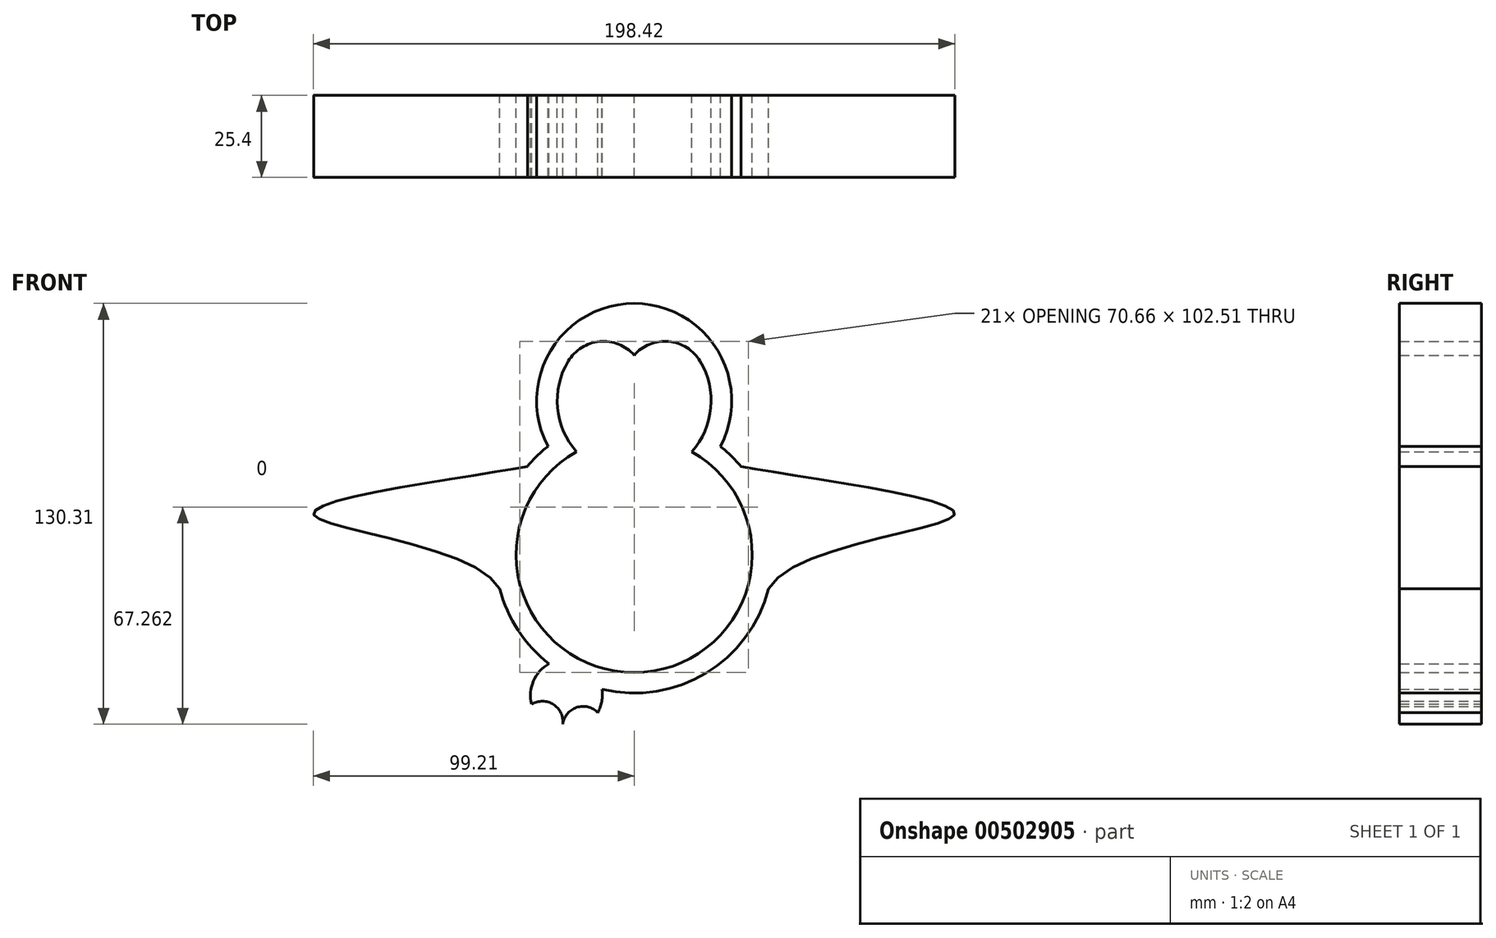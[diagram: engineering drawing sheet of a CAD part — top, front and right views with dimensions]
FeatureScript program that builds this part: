
annotation { "Feature Type Name" : "Feature", "Feature Type Description" : "" }
export const myFeature = defineFeature(function(context is Context, id is Id, definition is map)
    precondition{}
    {
        {
            var Q0;
            Q0=qCreatedBy(makeId("Front.planeOp"),FACE);
            var sketch = newSketch(context, id + "F0", { "sketchPlane" : qUnion([Q0])});
            skArc(sketch, "E0", {"start": v(26.68, 20.85) * mm, "mid": v(0, 65.09) * mm, "end": v(-26.68, 20.85) * mm});
            skArc(sketch, "E1", {"start": v(-26.68, 20.85) * mm, "mid": v(0, -55.56) * mm, "end": v(26.68, 20.85) * mm});
            skArc(sketch, "E2", {"start": v(-26.39, -46.48) * mm, "mid": v(-31.18, -51.83) * mm, "end": v(-31.7, -59) * mm});
            skPoint(sketch, "E3", {"position": v(-40.94, 0) * mm});
            skPoint(sketch, "E4", {"position": v(-91.74, 0) * mm});
            skArc(sketch, "E5.0", {"start": v(17.84, 19.16) * mm, "mid": v(23.71, 32.75) * mm, "end": v(20.41, 47.2) * mm});
            skArc(sketch, "E5.1", {"start": v(-17.84, 19.16) * mm, "mid": v(0, -49.21) * mm, "end": v(17.84, 19.16) * mm});
            skArc(sketch, "E6", {"start": v(0, 49.05) * mm, "mid": v(-10.68, 53.3) * mm, "end": v(-20.41, 47.2) * mm});
            skArc(sketch, "E7.MirrorC", {"start": v(0, 49.05) * mm, "mid": v(10.68, 53.3) * mm, "end": v(20.41, 47.2) * mm});
            skArc(sketch, "E8.trimOffspring", {"start": v(-20.41, 47.2) * mm, "mid": v(-23.71, 32.75) * mm, "end": v(-17.84, 19.16) * mm});
            skArc(sketch, "E9", {"start": v(-22.1, -65.22) * mm, "mid": v(-24.95, -59.1) * mm, "end": v(-31.7, -59) * mm});
            skArc(sketch, "E10", {"start": v(-11.25, -61.6) * mm, "mid": v(-17.82, -60) * mm, "end": v(-22.1, -65.22) * mm});
            skArc(sketch, "E11.trimOffspring", {"start": v(-11.25, -61.6) * mm, "mid": v(-10, -58.1) * mm, "end": v(-9.99, -54.38) * mm});
            skArc(sketch, "E12.trimOffspring", {"start": v(-22.67, -67.15) * mm, "mid": v(-22.35, -67.2) * mm, "end": v(-22.04, -67.23) * mm});
            skArc(sketch, "E13.MirrorCS", {"start": v(11.25, -61.6) * mm, "mid": v(10, -58.1) * mm, "end": v(9.99, -54.38) * mm});
            skArc(sketch, "E14.MirrorCS", {"start": v(11.25, -61.6) * mm, "mid": v(17.82, -60) * mm, "end": v(22.1, -65.22) * mm});
            skArc(sketch, "E15.MirrorCS", {"start": v(22.1, -65.22) * mm, "mid": v(24.95, -59.1) * mm, "end": v(31.7, -59) * mm});
            skArc(sketch, "E16.MirrorCS", {"start": v(26.39, -46.48) * mm, "mid": v(31.18, -51.83) * mm, "end": v(31.7, -59) * mm});
            skPoint(sketch, "E17", {"position": v(99.2, 0) * mm});
            skFitSpline(sketch, "E18", {"points": [v(33.02, 14.63) * mm, v(99.2, 0) * mm, v(41.55, -23.24) * mm], "startDerivative": vector(82.1, -16.26) * mm, "endDerivative": vector(-46.32, -85.17) * mm});
            skFitSpline(sketch, "E19.MirrorCS", {"points": [v(-33.02, 14.63) * mm, v(-99.2, 0) * mm, v(-41.55, -23.24) * mm], "startDerivative": vector(-82.1, -16.26) * mm, "endDerivative": vector(46.32, -85.17) * mm});
            skSolve(sketch);
        }
        {
            var Q0;
            {var subQ0=sQuery(id+"F0.wireOp",EDGE,"3274d125-688d-4c9a-ac35-9dc234a8c241");Q0=makeQuery(id+"F0.imprint","IMPRINT",FACE,{"disambiguationData":[TD([[makeQuery(id+"F0.imprint","IMPRINT",EDGE,{"derivedFrom":subQ0}),1.0]])]});}
            var Q1;
            {var subQ1=sQuery(id+"F0.wireOp",EDGE,"E0");Q1=makeQuery(id+"F0.imprint","IMPRINT",FACE,{"disambiguationData":[TD([[makeQuery(id+"F0.imprint","IMPRINT",EDGE,{"derivedFrom":subQ1}),1.0]])]});}
            var Q2;
            {var subQ0=sQuery(id+"F0.wireOp",EDGE,"3331a01e-69a7-4aaf-bf19-6445314629bc0.MirrorCS");Q2=makeQuery(id+"F0.imprint","IMPRINT",FACE,{"disambiguationData":[TD([[makeQuery(id+"F0.imprint","IMPRINT",EDGE,{"derivedFrom":subQ0}),-1.0]])]});}
            var Q3;
            {var subQ0=sQuery(id+"F0.wireOp",EDGE,"E13.MirrorCS");Q3=makeQuery(id+"F0.imprint","IMPRINT",FACE,{"disambiguationData":[TD([[makeQuery(id+"F0.imprint","IMPRINT",EDGE,{"derivedFrom":subQ0}),-1.0]])]});}
            var Q4;
            {var subQ0=sQuery(id+"F0.wireOp",EDGE,"E2");Q4=makeQuery(id+"F0.imprint","IMPRINT",FACE,{"disambiguationData":[TD([[makeQuery(id+"F0.imprint","IMPRINT",EDGE,{"derivedFrom":subQ0}),1.0]])]});}
            var Q5;
            {var subQ0=sQuery(id+"F0.wireOp",EDGE,"E18");Q5=makeQuery(id+"F0.imprint","IMPRINT",FACE,{"disambiguationData":[TD([[makeQuery(id+"F0.imprint","IMPRINT",EDGE,{"derivedFrom":subQ0}),-1.0]])]});}
            var Q6;
            {var subQ0=sQuery(id+"F0.wireOp",EDGE,"E19.MirrorCS");Q6=makeQuery(id+"F0.imprint","IMPRINT",FACE,{"disambiguationData":[TD([[makeQuery(id+"F0.imprint","IMPRINT",EDGE,{"derivedFrom":subQ0}),1.0]])]});}
            extrude(context, id + "F1", {"entities" : qUnion([Q0, Q1, Q2, Q3, Q4, Q5, Q6]), "depth" : 25.4 * mm});
        }
    });
